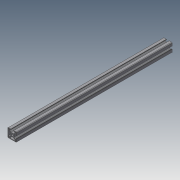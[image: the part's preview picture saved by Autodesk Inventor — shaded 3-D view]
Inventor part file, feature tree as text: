
AUTODESK INVENTOR PART (.ipt)
format: ipt  version: 2020.3 (Build 243373000, 373)  size: 311,808 bytes
history: native  units: in
note: dims shown in document units (in); Inventor stores cm internally (conversion verified against a paired STEP export)
features: extrude x1, sketch x1, projected_geometry x1, other x1
ambient origin geometry x8: Origin, YZ Plane, XZ Plane, XY Plane, X Axis, Y Axis, Z Axis, Center Point
bodies: Solid1 (feature_tree)
feature tree (4):
  extrude  "Extrusion1"  [1 undecoded]
  sketch  "Sketch1"  dims[d0=20.6299in d1=0.0in]
  projected_geometry  "Projected Loop1"
  other  "Boss-Extrude1"
note: 1 required parameter value undecoded (feature->parameter linkage not recoverable at this tier; creation-order binding heuristic only, values carry confidence <= 0.55)
